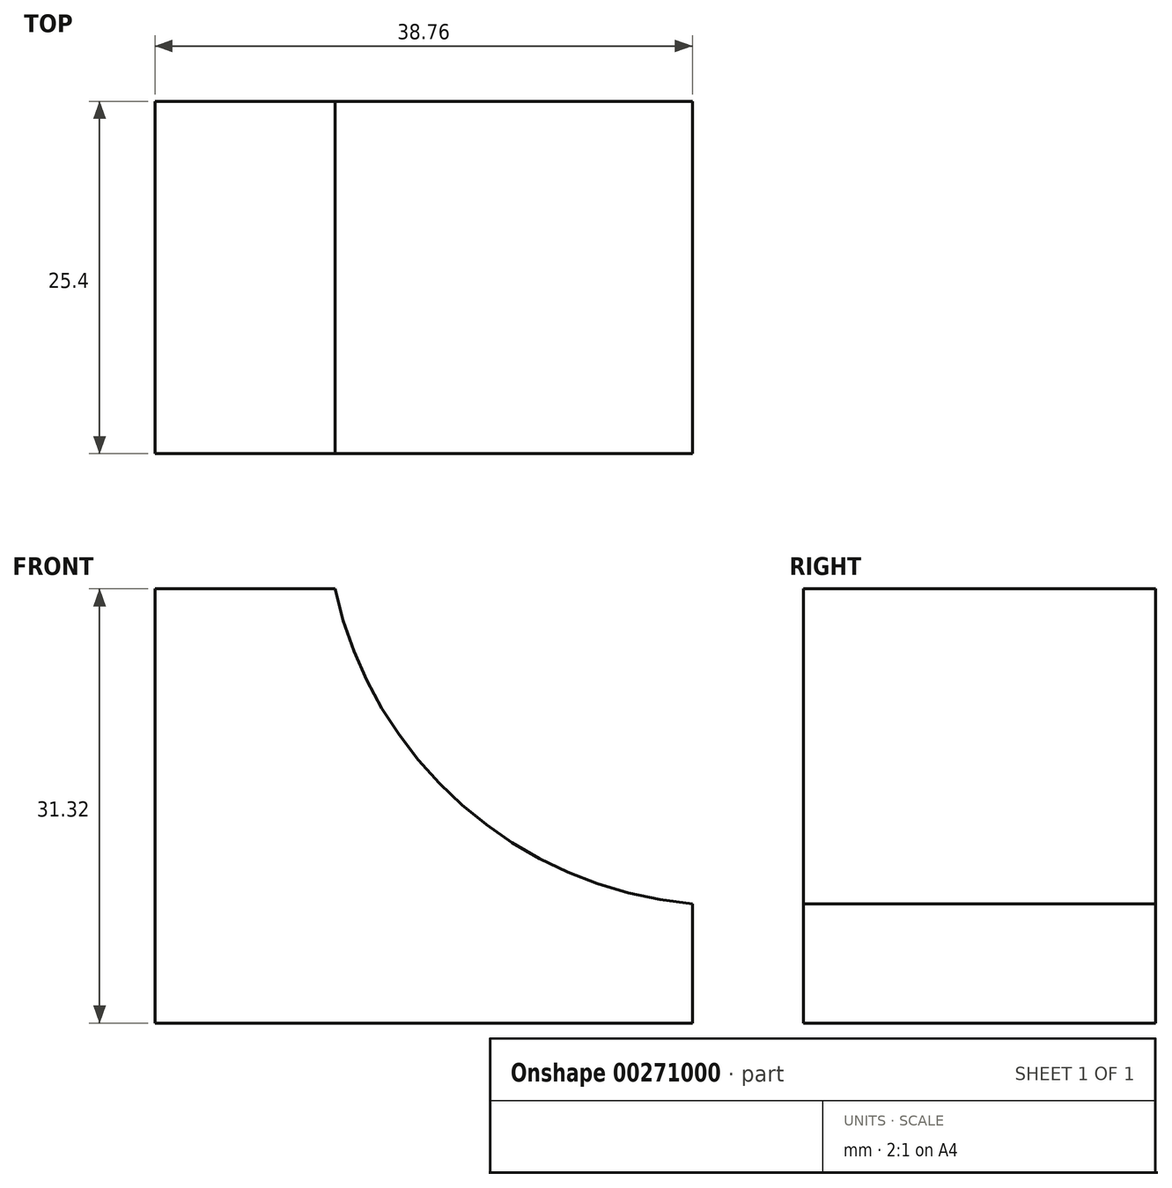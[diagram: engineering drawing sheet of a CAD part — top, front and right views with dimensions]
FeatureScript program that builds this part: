
annotation { "Feature Type Name" : "Feature", "Feature Type Description" : "" }
export const myFeature = defineFeature(function(context is Context, id is Id, definition is map)
    precondition{}
    {
        {
            var Q0;
            Q0=qCreatedBy(makeId("Front.planeOp"),FACE);
            var sketch = newSketch(context, id + "F0", { "sketchPlane" : qUnion([Q0])});
            skLineSegment(sketch, "E0", {"start": v(0, 0) * mm, "end": v(-38.76, 0) * mm});
            skLineSegment(sketch, "E1", {"start": v(-38.76, 0) * mm, "end": v(-38.76, 31.32) * mm});
            skLineSegment(sketch, "E2", {"start": v(-38.76, 31.32) * mm, "end": v(-25.78, 31.32) * mm});
            skLineSegment(sketch, "E3", {"start": v(0, 0) * mm, "end": v(0, 8.6) * mm});
            skArc(sketch, "E4", {"start": v(-25.78, 31.32) * mm, "mid": v(-16.62, 15.73) * mm, "end": v(0, 8.6) * mm});
            skSolve(sketch);
        }
        {
            var Q0;
            Q0 = qSketchRegion(id + "F0", true);
            extrude(context, id + "F1", {"entities" : qUnion([Q0]), "depth" : 25.4 * mm});
        }
    });
